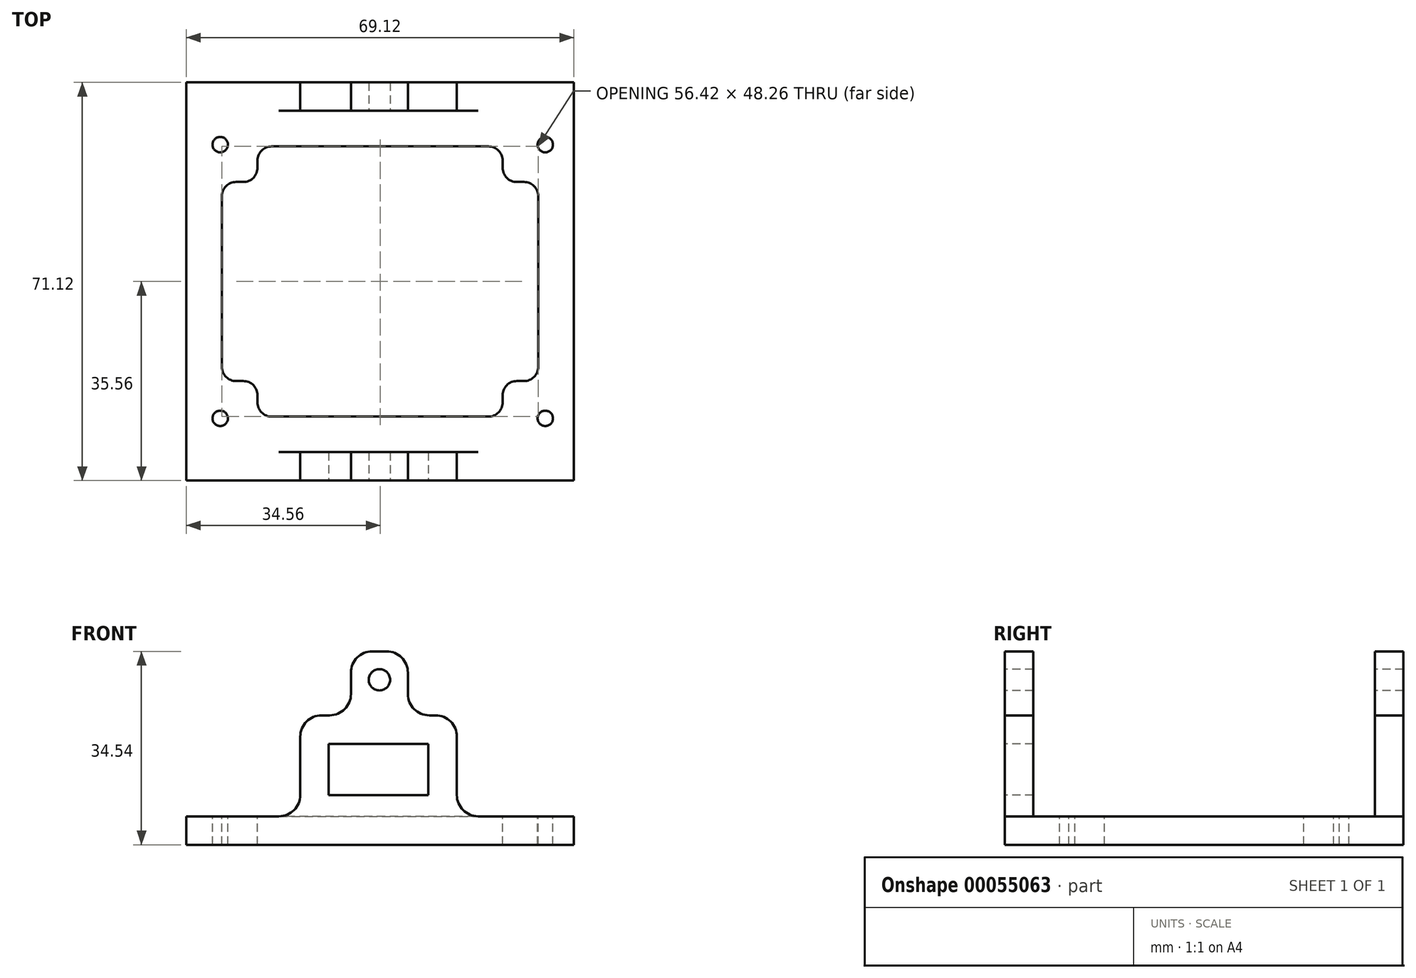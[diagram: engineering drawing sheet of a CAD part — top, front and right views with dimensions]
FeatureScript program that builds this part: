
annotation { "Feature Type Name" : "Feature", "Feature Type Description" : "" }
export const myFeature = defineFeature(function(context is Context, id is Id, definition is map)
    precondition{}
    {
        {
            var Q0;
            Q0=qCreatedBy(makeId("Top.planeOp"),FACE);
            var sketch = newSketch(context, id + "F0", { "sketchPlane" : qUnion([Q0])});
            skLineSegment(sketch, "E0.bottom", {"start": v(0, 0) * mm, "end": v(85.1, 0) * mm, "construction": true});
            skLineSegment(sketch, "E0.top", {"start": v(0, 55.88) * mm, "end": v(85.1, 55.88) * mm, "construction": true});
            skLineSegment(sketch, "E0.left", {"start": v(0, 0) * mm, "end": v(0, 55.88) * mm, "construction": true});
            skLineSegment(sketch, "E0.right", {"start": v(85.1, 0) * mm, "end": v(85.1, 55.88) * mm, "construction": true});
            skLineSegment(sketch, "E1", {"start": v(85.1, 54.61) * mm, "end": v(87.38, 54.61) * mm, "construction": true});
            skLineSegment(sketch, "E2", {"start": v(87.38, 54.61) * mm, "end": v(87.38, 2.29) * mm, "construction": true});
            skLineSegment(sketch, "E3", {"start": v(87.38, 2.29) * mm, "end": v(85.1, 2.29) * mm, "construction": true});
            skLineSegment(sketch, "E4", {"start": v(57.02, 0) * mm, "end": v(57.02, -2.29) * mm, "construction": true});
            skLineSegment(sketch, "E5", {"start": v(57.02, -2.29) * mm, "end": v(50.17, -2.29) * mm, "construction": true});
            skLineSegment(sketch, "E6", {"start": v(50.17, -2.29) * mm, "end": v(50.17, 0) * mm, "construction": true});
            skLineSegment(sketch, "E7", {"start": v(39.37, 0) * mm, "end": v(39.37, -0.76) * mm, "construction": true});
            skLineSegment(sketch, "E8", {"start": v(39.37, -0.76) * mm, "end": v(24.13, -0.76) * mm, "construction": true});
            skLineSegment(sketch, "E9", {"start": v(24.13, -0.76) * mm, "end": v(24.13, 0) * mm, "construction": true});
            skLineSegment(sketch, "E10", {"start": v(14.99, 0) * mm, "end": v(14.99, -1.27) * mm, "construction": true});
            skLineSegment(sketch, "E11", {"start": v(14.99, -1.27) * mm, "end": v(6.86, -1.27) * mm, "construction": true});
            skLineSegment(sketch, "E12", {"start": v(6.86, -1.27) * mm, "end": v(6.86, 0) * mm, "construction": true});
            skLineSegment(sketch, "E13", {"start": v(0, 33.53) * mm, "end": v(-2.54, 33.53) * mm, "construction": true});
            skLineSegment(sketch, "E14", {"start": v(-2.54, 33.53) * mm, "end": v(-2.54, 22.35) * mm, "construction": true});
            skLineSegment(sketch, "E15", {"start": v(-2.54, 22.35) * mm, "end": v(0, 22.35) * mm, "construction": true});
            skCircle(sketch, "E16", {"center": v(3.5, 52.38) * mm, "radius": 1.38 * mm});
            skCircle(sketch, "E17", {"center": v(3.5, 3.5) * mm, "radius": 1.38 * mm});
            skCircle(sketch, "E18", {"center": v(61.5, 3.5) * mm, "radius": 1.38 * mm});
            skCircle(sketch, "E19", {"center": v(61.5, 52.38) * mm, "radius": 1.38 * mm});
            skLineSegment(sketch, "E20.bottom", {"start": v(-2.54, -2.54) * mm, "end": v(87.63, -2.54) * mm});
            skLineSegment(sketch, "E20.top", {"start": v(-2.54, 58.42) * mm, "end": v(87.63, 58.42) * mm});
            skLineSegment(sketch, "E20.left", {"start": v(-2.54, -2.54) * mm, "end": v(-2.54, 58.42) * mm});
            skLineSegment(sketch, "E20.right", {"start": v(87.63, -2.54) * mm, "end": v(87.63, 58.42) * mm});
            skLineSegment(sketch, "E21.0", {"start": v(-7.62, -7.62) * mm, "end": v(92.71, -7.62) * mm});
            skLineSegment(sketch, "E21.1", {"start": v(-7.62, -7.62) * mm, "end": v(-7.62, 63.5) * mm});
            skLineSegment(sketch, "E21.2", {"start": v(-7.62, 63.5) * mm, "end": v(92.71, 63.5) * mm});
            skLineSegment(sketch, "E21.3", {"start": v(92.71, -7.62) * mm, "end": v(92.71, 63.5) * mm});
            skSolve(sketch);
        }
        {
            var Q0;
            Q0=makeQuery(id+"F0.imprint","IMPRINT",FACE,{"disambiguationData":[TD([[makeQuery(id+"F0.imprint","IMPRINT",EDGE,{"derivedFrom":sQuery(id+"F0.wireOp",EDGE,"E20.bottom")}),-1.0]])]});
            extrude(context, id + "F1", {"entities" : qUnion([Q0]), "oppositeDirection" : true, "depth" : 5.08 * mm});
        }
        {
            var Q0;
            Q0=makeQuery(id+"F1.opExtrude","CAP_FACE",FACE,{"disambiguationData":[OSD([sQuery(id+"F0.wireOp",EDGE,"E20.bottom"),sQuery(id+"F0.wireOp",EDGE,"E20.top"),sQuery(id+"F0.wireOp",EDGE,"E20.left"),sQuery(id+"F0.wireOp",EDGE,"E20.right"),sQuery(id+"F0.wireOp",EDGE,"E21.0"),sQuery(id+"F0.wireOp",EDGE,"E21.1"),sQuery(id+"F0.wireOp",EDGE,"E21.2"),sQuery(id+"F0.wireOp",EDGE,"E21.3")])],"isStart":false});
            var sketch = newSketch(context, id + "F2", { "sketchPlane" : qUnion([Q0])});
            skLineSegment(sketch, "E22.bottom", {"start": v(-7.62, 7.62) * mm, "end": v(92.71, 7.62) * mm});
            skLineSegment(sketch, "E22.top", {"start": v(-7.62, -63.5) * mm, "end": v(92.71, -63.5) * mm});
            skLineSegment(sketch, "E22.left", {"start": v(-7.62, 7.62) * mm, "end": v(-7.62, -63.5) * mm});
            skLineSegment(sketch, "E22.right", {"start": v(92.71, 7.62) * mm, "end": v(92.71, -63.5) * mm});
            skSolve(sketch);
        }
        {
            var Q0;
            Q0=qSketchRegion(id+"F2",true);
            extrude(context, id + "F3", {"entities" : qUnion([Q0]), "operationType" : NewBodyOperationType.ADD, "depth" : 5.08 * mm});
        }
        {
            var Q0;
            Q0=makeQuery(id+"F0.imprint","IMPRINT",FACE,{"disambiguationData":[TD([[makeQuery(id+"F0.imprint","IMPRINT",EDGE,{"derivedFrom":sQuery(id+"F0.wireOp",EDGE,"E16")}),1.0]])]});
            var Q1;
            Q1=makeQuery(id+"F0.imprint","IMPRINT",FACE,{"disambiguationData":[TD([[makeQuery(id+"F0.imprint","IMPRINT",EDGE,{"derivedFrom":sQuery(id+"F0.wireOp",EDGE,"E19")}),1.0]])]});
            var Q2;
            Q2=makeQuery(id+"F0.imprint","IMPRINT",FACE,{"disambiguationData":[TD([[makeQuery(id+"F0.imprint","IMPRINT",EDGE,{"derivedFrom":sQuery(id+"F0.wireOp",EDGE,"E18")}),1.0]])]});
            var Q3;
            Q3=makeQuery(id+"F0.imprint","IMPRINT",FACE,{"disambiguationData":[TD([[makeQuery(id+"F0.imprint","IMPRINT",EDGE,{"derivedFrom":sQuery(id+"F0.wireOp",EDGE,"E17")}),1.0]])]});
            extrude(context, id + "F4", {"entities" : qUnion([Q0, Q1, Q2, Q3]), "operationType" : NewBodyOperationType.REMOVE, "oppositeDirection" : true, "depth" : 25.4 * mm});
        }
        {
            var Q0;
            Q0=makeQuery(id+"F3.opExtrude","CAP_FACE",FACE,{"disambiguationData":[OSD([sQuery(id+"F2.wireOp",EDGE,"E22.bottom"),sQuery(id+"F2.wireOp",EDGE,"E22.top"),sQuery(id+"F2.wireOp",EDGE,"E22.left"),sQuery(id+"F2.wireOp",EDGE,"E22.right")])],"isStart":true});
            var sketch = newSketch(context, id + "F5", { "sketchPlane" : qUnion([Q0])});
            skCircle(sketch, "E23", {"center": v(3.5, 52.38) * mm, "radius": 3.1 * mm});
            skCircle(sketch, "E24", {"center": v(61.5, 52.38) * mm, "radius": 3.1 * mm});
            skCircle(sketch, "E25", {"center": v(61.5, 3.5) * mm, "radius": 3.1 * mm});
            skCircle(sketch, "E26", {"center": v(3.5, 3.5) * mm, "radius": 3.1 * mm});
            skCircle(sketch, "E27", {"center": v(3.5, 52.38) * mm, "radius": 1.38 * mm});
            skCircle(sketch, "E28", {"center": v(3.5, 3.5) * mm, "radius": 1.38 * mm});
            skCircle(sketch, "E29", {"center": v(61.5, 3.5) * mm, "radius": 1.38 * mm});
            skCircle(sketch, "E30", {"center": v(61.5, 52.38) * mm, "radius": 1.38 * mm});
            skSolve(sketch);
        }
        {
            var Q0;
            Q0=qSketchRegion(id+"F5",true);
            extrude(context, id + "F6", {"entities" : qUnion([Q0]), "operationType" : NewBodyOperationType.ADD, "depth" : 3.56 * mm});
        }
        {
            var Q0;
            Q0=makeQuery(id+"F0.imprint","IMPRINT",FACE,{"disambiguationData":[TD([[makeQuery(id+"F0.imprint","IMPRINT",EDGE,{"derivedFrom":sQuery(id+"F0.wireOp",EDGE,"E20.bottom")}),-1.0]])]});
            extrude(context, id + "F7", {"entities" : qUnion([Q0]), "operationType" : NewBodyOperationType.ADD, "depth" : 37.6 * mm});
        }
        {
            var Q0;
            {var subQ0=sQuery(id+"F0.wireOp",EDGE,"E21.1");Q0=makeQuery(id+"F7.boolean.opBoolean","MERGE",FACE,{"derivedFrom":[makeQuery(id+"F3.boolean.opBoolean","MERGE",FACE,{"derivedFrom":[makeQuery(id+"F1.opExtrude","SWEPT_FACE",FACE,{"disambiguationData":[OSD([subQ0])]}),makeQuery(id+"F3.opExtrude","SWEPT_FACE",FACE,{"disambiguationData":[OSD([sQuery(id+"F2.wireOp",EDGE,"E22.left")])]})]}),makeQuery(id+"F7.opExtrude","SWEPT_FACE",FACE,{"disambiguationData":[OSD([subQ0])]})]});}
            var sketch = newSketch(context, id + "F8", { "sketchPlane" : qUnion([Q0])});
            skLineSegment(sketch, "E31.rect.bottom", {"start": v(-21.08, -3.81) * mm, "end": v(-34.8, -3.81) * mm});
            skLineSegment(sketch, "E31.rect.top", {"start": v(-21.08, -0.25) * mm, "end": v(-34.8, -0.25) * mm});
            skLineSegment(sketch, "E31.rect.left", {"start": v(-21.08, -3.8) * mm, "end": v(-21.08, -0.25) * mm});
            skLineSegment(sketch, "E31.rect.right", {"start": v(-34.8, -3.81) * mm, "end": v(-34.8, -0.25) * mm});
            skPoint(sketch, "E31.rect.middle", {"position": v(-27.94, -2.03) * mm});
            skLineSegment(sketch, "E32.bottom", {"start": v(-33.53, -1.52) * mm, "end": v(-22.35, -1.52) * mm, "construction": true});
            skLineSegment(sketch, "E32.top", {"start": v(-33.53, -2.54) * mm, "end": v(-22.35, -2.54) * mm, "construction": true});
            skLineSegment(sketch, "E32.left", {"start": v(-33.53, -1.52) * mm, "end": v(-33.53, -2.54) * mm, "construction": true});
            skLineSegment(sketch, "E32.right", {"start": v(-22.35, -1.52) * mm, "end": v(-22.35, -2.54) * mm, "construction": true});
            skSolve(sketch);
        }
        {
            var Q0;
            Q0=qSketchRegion(id+"F8",true);
            extrude(context, id + "F9", {"entities" : qUnion([Q0]), "operationType" : NewBodyOperationType.REMOVE, "endBound" : BoundingType.UP_TO_NEXT, "oppositeDirection" : true, "depth" : 25.4 * mm});
        }
        {
            var Q0;
            {var subQ0=sQuery(id+"F0.wireOp",EDGE,"E21.0");Q0=makeQuery(id+"F7.boolean.opBoolean","MERGE",FACE,{"derivedFrom":[makeQuery(id+"F3.boolean.opBoolean","MERGE",FACE,{"derivedFrom":[makeQuery(id+"F1.opExtrude","SWEPT_FACE",FACE,{"disambiguationData":[OSD([subQ0])]}),makeQuery(id+"F3.opExtrude","SWEPT_FACE",FACE,{"disambiguationData":[OSD([sQuery(id+"F2.wireOp",EDGE,"E22.bottom")])]})]}),makeQuery(id+"F7.opExtrude","SWEPT_FACE",FACE,{"disambiguationData":[OSD([subQ0])]})]});}
            var sketch = newSketch(context, id + "F10", { "sketchPlane" : qUnion([Q0])});
            skLineSegment(sketch, "E33.bottom", {"start": v(6.86, 3.18) * mm, "end": v(14.99, 3.18) * mm, "construction": true});
            skLineSegment(sketch, "E33.top", {"start": v(6.86, 0) * mm, "end": v(14.99, 0) * mm, "construction": true});
            skLineSegment(sketch, "E33.left", {"start": v(6.86, 3.18) * mm, "end": v(6.86, 0) * mm, "construction": true});
            skLineSegment(sketch, "E33.right", {"start": v(14.99, 3.18) * mm, "end": v(14.99, 0) * mm, "construction": true});
            skLineSegment(sketch, "E34.bottom", {"start": v(24.13, 6.6) * mm, "end": v(39.37, 6.6) * mm, "construction": true});
            skLineSegment(sketch, "E34.top", {"start": v(24.13, 0) * mm, "end": v(39.37, 0) * mm, "construction": true});
            skLineSegment(sketch, "E34.left", {"start": v(24.13, 6.6) * mm, "end": v(24.13, 0) * mm, "construction": true});
            skLineSegment(sketch, "E34.right", {"start": v(39.37, 6.6) * mm, "end": v(39.37, 0) * mm, "construction": true});
            skLineSegment(sketch, "E35.bottom", {"start": v(50.17, 6.35) * mm, "end": v(57.02, 6.35) * mm, "construction": true});
            skLineSegment(sketch, "E35.top", {"start": v(50.17, 0) * mm, "end": v(57.02, 0) * mm, "construction": true});
            skLineSegment(sketch, "E35.left", {"start": v(50.17, 6.35) * mm, "end": v(50.17, 0) * mm, "construction": true});
            skLineSegment(sketch, "E35.right", {"start": v(57.02, 6.35) * mm, "end": v(57.02, 0) * mm, "construction": true});
            skLineSegment(sketch, "E36.bottom", {"start": v(16.26, 4.45) * mm, "end": v(5.59, 4.45) * mm});
            skLineSegment(sketch, "E36.top", {"start": v(16.26, -1.27) * mm, "end": v(5.59, -1.27) * mm});
            skLineSegment(sketch, "E36.left", {"start": v(16.26, 4.45) * mm, "end": v(16.26, -1.27) * mm});
            skLineSegment(sketch, "E36.right", {"start": v(5.59, 4.45) * mm, "end": v(5.59, -1.27) * mm});
            skLineSegment(sketch, "E37.bottom", {"start": v(22.86, 7.87) * mm, "end": v(40.64, 7.87) * mm});
            skLineSegment(sketch, "E37.top", {"start": v(22.86, -1.27) * mm, "end": v(40.64, -1.27) * mm});
            skLineSegment(sketch, "E37.left", {"start": v(22.86, 7.87) * mm, "end": v(22.86, -1.27) * mm});
            skLineSegment(sketch, "E37.right", {"start": v(40.64, 7.87) * mm, "end": v(40.64, -1.27) * mm});
            skLineSegment(sketch, "E38.bottom", {"start": v(48.9, 7.62) * mm, "end": v(58.3, 7.62) * mm});
            skLineSegment(sketch, "E38.top", {"start": v(48.9, -1.27) * mm, "end": v(58.3, -1.27) * mm});
            skLineSegment(sketch, "E38.left", {"start": v(48.9, 7.62) * mm, "end": v(48.9, -1.27) * mm});
            skLineSegment(sketch, "E38.right", {"start": v(58.3, 7.62) * mm, "end": v(58.3, -1.27) * mm});
            skPoint(sketch, "E39", {"position": v(14.99, 1.59) * mm});
            skPoint(sketch, "E40", {"position": v(10.92, 0) * mm});
            skPoint(sketch, "E41", {"position": v(10.92, -1.27) * mm});
            skPoint(sketch, "E42", {"position": v(16.26, 1.59) * mm});
            skPoint(sketch, "E43", {"position": v(22.86, 3.3) * mm});
            skPoint(sketch, "E44", {"position": v(31.75, -1.27) * mm});
            skPoint(sketch, "E45", {"position": v(31.75, 0) * mm});
            skPoint(sketch, "E46", {"position": v(24.13, 3.3) * mm});
            skPoint(sketch, "E47", {"position": v(58.3, 3.18) * mm});
            skPoint(sketch, "E48", {"position": v(53.6, -1.27) * mm});
            skPoint(sketch, "E49", {"position": v(53.6, 0) * mm});
            skPoint(sketch, "E50", {"position": v(57.02, 3.18) * mm});
            skLineSegment(sketch, "E51", {"start": v(14.99, 0) * mm, "end": v(14.99, -1.27) * mm, "construction": true});
            skLineSegment(sketch, "E52", {"start": v(14.99, 0) * mm, "end": v(16.26, 0) * mm, "construction": true});
            skLineSegment(sketch, "E53", {"start": v(24.13, 0) * mm, "end": v(22.86, 0) * mm, "construction": true});
            skLineSegment(sketch, "E54", {"start": v(24.13, 0) * mm, "end": v(24.13, -1.27) * mm, "construction": true});
            skLineSegment(sketch, "E55", {"start": v(50.17, 0) * mm, "end": v(48.9, 0) * mm, "construction": true});
            skLineSegment(sketch, "E56", {"start": v(50.17, 0) * mm, "end": v(50.17, -1.27) * mm, "construction": true});
            skSolve(sketch);
        }
        {
            var Q0;
            Q0=qSketchRegion(id+"F10",true);
            extrude(context, id + "F11", {"entities" : qUnion([Q0]), "operationType" : NewBodyOperationType.REMOVE, "endBound" : BoundingType.UP_TO_NEXT, "oppositeDirection" : true, "depth" : 25.4 * mm});
        }
        {
            var Q0;
            {var subQ0=sQuery(id+"F0.wireOp",EDGE,"E21.3");Q0=makeQuery(id+"F7.boolean.opBoolean","MERGE",FACE,{"derivedFrom":[makeQuery(id+"F3.boolean.opBoolean","MERGE",FACE,{"derivedFrom":[makeQuery(id+"F1.opExtrude","SWEPT_FACE",FACE,{"disambiguationData":[OSD([subQ0])]}),makeQuery(id+"F3.opExtrude","SWEPT_FACE",FACE,{"disambiguationData":[OSD([sQuery(id+"F2.wireOp",EDGE,"E22.right")])]})]}),makeQuery(id+"F7.opExtrude","SWEPT_FACE",FACE,{"disambiguationData":[OSD([subQ0])]})]});}
            var sketch = newSketch(context, id + "F12", { "sketchPlane" : qUnion([Q0])});
            skLineSegment(sketch, "E57.bottom", {"start": v(2.54, 13.72) * mm, "end": v(18.54, 13.72) * mm, "construction": true});
            skLineSegment(sketch, "E57.top", {"start": v(2.54, 0) * mm, "end": v(18.54, 0) * mm, "construction": true});
            skLineSegment(sketch, "E57.left", {"start": v(2.54, 13.72) * mm, "end": v(2.54, 0) * mm, "construction": true});
            skLineSegment(sketch, "E57.right", {"start": v(18.54, 13.72) * mm, "end": v(18.54, 0) * mm, "construction": true});
            skLineSegment(sketch, "E58.bottom", {"start": v(21.44, 16.26) * mm, "end": v(36.68, 16.26) * mm, "construction": true});
            skLineSegment(sketch, "E58.top", {"start": v(21.44, 0) * mm, "end": v(36.68, 0) * mm, "construction": true});
            skLineSegment(sketch, "E58.left", {"start": v(21.44, 16.26) * mm, "end": v(21.44, 0) * mm, "construction": true});
            skLineSegment(sketch, "E58.right", {"start": v(36.68, 16.26) * mm, "end": v(36.68, 0) * mm, "construction": true});
            skLineSegment(sketch, "E59.bottom", {"start": v(39.22, 16.26) * mm, "end": v(54.46, 16.26) * mm, "construction": true});
            skLineSegment(sketch, "E59.top", {"start": v(39.22, 0) * mm, "end": v(54.46, 0) * mm, "construction": true});
            skLineSegment(sketch, "E59.left", {"start": v(39.22, 16.26) * mm, "end": v(39.22, 0) * mm, "construction": true});
            skLineSegment(sketch, "E59.right", {"start": v(54.46, 16.26) * mm, "end": v(54.46, 0) * mm, "construction": true});
            skLineSegment(sketch, "E60.bottom", {"start": v(1.9, 16.9) * mm, "end": v(55.73, 16.9) * mm});
            skLineSegment(sketch, "E60.top", {"start": v(1.9, -1.27) * mm, "end": v(55.73, -1.27) * mm});
            skLineSegment(sketch, "E60.left", {"start": v(1.9, 16.9) * mm, "end": v(1.9, -1.27) * mm});
            skLineSegment(sketch, "E60.right", {"start": v(55.73, 16.9) * mm, "end": v(55.73, -1.27) * mm});
            skSolve(sketch);
        }
        {
            var Q0;
            Q0=qSketchRegion(id+"F12",true);
            extrude(context, id + "F13", {"entities" : qUnion([Q0]), "operationType" : NewBodyOperationType.REMOVE, "endBound" : BoundingType.UP_TO_NEXT, "oppositeDirection" : true, "depth" : 25.4 * mm});
        }
        {
            var Q0;
            {var subQ0=sQuery(id+"F0.wireOp",EDGE,"E21.0");Q0=makeQuery(id+"F7.boolean.opBoolean","MERGE",FACE,{"derivedFrom":[makeQuery(id+"F3.boolean.opBoolean","MERGE",FACE,{"derivedFrom":[makeQuery(id+"F1.opExtrude","SWEPT_FACE",FACE,{"disambiguationData":[OSD([subQ0])]}),makeQuery(id+"F3.opExtrude","SWEPT_FACE",FACE,{"disambiguationData":[OSD([sQuery(id+"F2.wireOp",EDGE,"E22.bottom")])]})]}),makeQuery(id+"F7.opExtrude","SWEPT_FACE",FACE,{"disambiguationData":[OSD([subQ0])]})]});}
            var sketch = newSketch(context, id + "F14", { "sketchPlane" : qUnion([Q0])});
            skCircle(sketch, "E61", {"center": v(31.9, 19.3) * mm, "radius": 1.9 * mm});
            skSolve(sketch);
        }
        {
            var Q0;
            Q0=qSketchRegion(id+"F14",true);
            extrude(context, id + "F15", {"entities" : qUnion([Q0]), "operationType" : NewBodyOperationType.REMOVE, "endBound" : BoundingType.THROUGH_ALL, "oppositeDirection" : true, "depth" : 25.4 * mm});
        }
        {
            var Q0;
            {var subQ0=sQuery(id+"F0.wireOp",EDGE,"E21.0");Q0=makeQuery(id+"F7.boolean.opBoolean","MERGE",FACE,{"derivedFrom":[makeQuery(id+"F3.boolean.opBoolean","MERGE",FACE,{"derivedFrom":[makeQuery(id+"F1.opExtrude","SWEPT_FACE",FACE,{"disambiguationData":[OSD([subQ0])]}),makeQuery(id+"F3.opExtrude","SWEPT_FACE",FACE,{"disambiguationData":[OSD([sQuery(id+"F2.wireOp",EDGE,"E22.bottom")])]})]}),makeQuery(id+"F7.opExtrude","SWEPT_FACE",FACE,{"disambiguationData":[OSD([subQ0])]})]});}
            var sketch = newSketch(context, id + "F16", { "sketchPlane" : qUnion([Q0])});
            skLineSegment(sketch, "E62", {"start": v(66.58, -10.16) * mm, "end": v(66.58, -5.08) * mm});
            skLineSegment(sketch, "E63", {"start": v(-2.54, -10.16) * mm, "end": v(-2.54, -5.08) * mm});
            skLineSegment(sketch, "E64", {"start": v(-2.54, -10.16) * mm, "end": v(-7.62, -10.16) * mm});
            skLineSegment(sketch, "E65", {"start": v(-7.62, -10.16) * mm, "end": v(-7.62, 37.6) * mm});
            skLineSegment(sketch, "E66", {"start": v(-7.62, 37.6) * mm, "end": v(92.71, 37.6) * mm});
            skLineSegment(sketch, "E67", {"start": v(92.71, 37.6) * mm, "end": v(92.71, -10.16) * mm});
            skLineSegment(sketch, "E68", {"start": v(92.71, -10.16) * mm, "end": v(66.58, -10.16) * mm});
            skLineSegment(sketch, "E69", {"start": v(-2.54, -5.08) * mm, "end": v(13.97, -5.08) * mm});
            skLineSegment(sketch, "E70", {"start": v(17.78, -1.27) * mm, "end": v(17.78, 9.14) * mm});
            skLineSegment(sketch, "E71", {"start": v(21.6, 12.95) * mm, "end": v(23.01, 12.95) * mm});
            skLineSegment(sketch, "E72", {"start": v(26.82, 16.76) * mm, "end": v(26.82, 20.57) * mm});
            skLineSegment(sketch, "E73", {"start": v(30.63, 24.38) * mm, "end": v(33.17, 24.38) * mm});
            skLineSegment(sketch, "E74", {"start": v(36.98, 20.57) * mm, "end": v(36.98, 16.76) * mm});
            skLineSegment(sketch, "E75", {"start": v(40.8, 12.95) * mm, "end": v(41.91, 12.95) * mm});
            skLineSegment(sketch, "E76", {"start": v(45.72, 9.14) * mm, "end": v(45.72, -1.27) * mm});
            skLineSegment(sketch, "E77", {"start": v(49.53, -5.08) * mm, "end": v(66.58, -5.08) * mm});
            skCircle(sketch, "E78", {"center": v(31.9, 19.3) * mm, "radius": 5.08 * mm, "construction": true});
            skPoint(sketch, "E79.visualSharp", {"position": v(17.78, -5.08) * mm});
            skArc(sketch, "E79.filletArc", {"start": v(13.97, -5.08) * mm, "mid": v(16.66, -3.96) * mm, "end": v(17.78, -1.27) * mm});
            skPoint(sketch, "E80.visualSharp", {"position": v(17.78, 12.95) * mm});
            skArc(sketch, "E80.filletArc", {"start": v(21.6, 12.95) * mm, "mid": v(18.9, 11.84) * mm, "end": v(17.78, 9.14) * mm});
            skPoint(sketch, "E81.visualSharp", {"position": v(26.82, 12.95) * mm});
            skArc(sketch, "E81.filletArc", {"start": v(23.01, 12.95) * mm, "mid": v(25.7, 14.07) * mm, "end": v(26.82, 16.76) * mm});
            skPoint(sketch, "E82.visualSharp", {"position": v(26.82, 24.38) * mm});
            skArc(sketch, "E82.filletArc", {"start": v(30.63, 24.38) * mm, "mid": v(27.94, 23.27) * mm, "end": v(26.82, 20.57) * mm});
            skPoint(sketch, "E83.visualSharp", {"position": v(36.98, 24.38) * mm});
            skArc(sketch, "E83.filletArc", {"start": v(36.98, 20.57) * mm, "mid": v(35.87, 23.27) * mm, "end": v(33.17, 24.38) * mm});
            skPoint(sketch, "E84.visualSharp", {"position": v(36.98, 12.95) * mm});
            skArc(sketch, "E84.filletArc", {"start": v(36.98, 16.76) * mm, "mid": v(38.1, 14.07) * mm, "end": v(40.8, 12.95) * mm});
            skPoint(sketch, "E85.visualSharp", {"position": v(45.72, 12.95) * mm});
            skArc(sketch, "E85.filletArc", {"start": v(45.72, 9.14) * mm, "mid": v(44.6, 11.84) * mm, "end": v(41.91, 12.95) * mm});
            skPoint(sketch, "E86.visualSharp", {"position": v(45.72, -5.08) * mm});
            skArc(sketch, "E86.filletArc", {"start": v(45.72, -1.27) * mm, "mid": v(46.84, -3.96) * mm, "end": v(49.53, -5.08) * mm});
            skSolve(sketch);
        }
        {
            var Q0;
            Q0 = qSketchRegion(id + "F16", true);
            extrude(context, id + "F17", {"entities" : qUnion([Q0]), "operationType" : NewBodyOperationType.REMOVE, "endBound" : BoundingType.THROUGH_ALL, "oppositeDirection" : true, "depth" : 25.4 * mm});
        }
        {
            var Q0;
            Q0=makeQuery(id+"F3.opExtrude","CAP_FACE",FACE,{"disambiguationData":[OSD([sQuery(id+"F2.wireOp",EDGE,"E22.bottom"),sQuery(id+"F2.wireOp",EDGE,"E22.top"),sQuery(id+"F2.wireOp",EDGE,"E22.left"),sQuery(id+"F2.wireOp",EDGE,"E22.right")])],"isStart":true});
            var sketch = newSketch(context, id + "F18", { "sketchPlane" : qUnion([Q0])});
            skLineSegment(sketch, "E87", {"start": v(57.7, 10.16) * mm, "end": v(56.42, 10.16) * mm});
            skLineSegment(sketch, "E88", {"start": v(53.88, 7.62) * mm, "end": v(53.88, 6.35) * mm});
            skLineSegment(sketch, "E89", {"start": v(51.34, 3.81) * mm, "end": v(12.7, 3.8) * mm});
            skLineSegment(sketch, "E90", {"start": v(10.16, 6.35) * mm, "end": v(10.16, 7.62) * mm});
            skLineSegment(sketch, "E91", {"start": v(7.62, 10.16) * mm, "end": v(6.35, 10.16) * mm});
            skLineSegment(sketch, "E92", {"start": v(3.81, 12.7) * mm, "end": v(3.81, 43.18) * mm});
            skLineSegment(sketch, "E93", {"start": v(6.35, 45.72) * mm, "end": v(7.62, 45.72) * mm});
            skLineSegment(sketch, "E94", {"start": v(10.16, 48.26) * mm, "end": v(10.16, 49.53) * mm});
            skLineSegment(sketch, "E95", {"start": v(12.7, 52.07) * mm, "end": v(51.34, 52.07) * mm});
            skLineSegment(sketch, "E96", {"start": v(53.88, 49.53) * mm, "end": v(53.88, 48.26) * mm});
            skLineSegment(sketch, "E97", {"start": v(56.42, 45.72) * mm, "end": v(57.7, 45.72) * mm});
            skLineSegment(sketch, "E98", {"start": v(60.23, 43.18) * mm, "end": v(60.23, 12.7) * mm});
            skLineSegment(sketch, "E99", {"start": v(3.8, 10.16) * mm, "end": v(-2.54, 10.16) * mm, "construction": true});
            skLineSegment(sketch, "E100", {"start": v(60.23, 10.16) * mm, "end": v(66.58, 10.16) * mm, "construction": true});
            skLineSegment(sketch, "E101", {"start": v(53.88, 52.07) * mm, "end": v(53.88, 58.42) * mm, "construction": true});
            skLineSegment(sketch, "E102", {"start": v(53.88, 3.8) * mm, "end": v(53.88, -2.54) * mm, "construction": true});
            skPoint(sketch, "E103.visualSharp", {"position": v(3.81, 45.72) * mm});
            skArc(sketch, "E103.filletArc", {"start": v(6.35, 45.72) * mm, "mid": v(4.55, 44.98) * mm, "end": v(3.8, 43.18) * mm});
            skPoint(sketch, "E104.visualSharp", {"position": v(10.16, 45.72) * mm});
            skArc(sketch, "E104.filletArc", {"start": v(7.62, 45.72) * mm, "mid": v(9.42, 46.46) * mm, "end": v(10.16, 48.26) * mm});
            skPoint(sketch, "E105.visualSharp", {"position": v(10.16, 52.07) * mm});
            skArc(sketch, "E105.filletArc", {"start": v(12.7, 52.07) * mm, "mid": v(10.9, 51.33) * mm, "end": v(10.16, 49.53) * mm});
            skPoint(sketch, "E106.visualSharp", {"position": v(53.88, 52.07) * mm});
            skArc(sketch, "E106.filletArc", {"start": v(53.88, 49.53) * mm, "mid": v(53.14, 51.33) * mm, "end": v(51.34, 52.07) * mm});
            skPoint(sketch, "E107.visualSharp", {"position": v(53.88, 45.72) * mm});
            skArc(sketch, "E107.filletArc", {"start": v(53.88, 48.26) * mm, "mid": v(54.62, 46.46) * mm, "end": v(56.42, 45.72) * mm});
            skPoint(sketch, "E108.visualSharp", {"position": v(60.23, 45.72) * mm});
            skArc(sketch, "E108.filletArc", {"start": v(60.23, 43.18) * mm, "mid": v(59.49, 44.98) * mm, "end": v(57.7, 45.72) * mm});
            skPoint(sketch, "E109.visualSharp", {"position": v(60.23, 10.16) * mm});
            skArc(sketch, "E109.filletArc", {"start": v(57.7, 10.16) * mm, "mid": v(59.49, 10.9) * mm, "end": v(60.23, 12.7) * mm});
            skPoint(sketch, "E110.visualSharp", {"position": v(53.88, 10.16) * mm});
            skArc(sketch, "E110.filletArc", {"start": v(56.42, 10.16) * mm, "mid": v(54.62, 9.42) * mm, "end": v(53.88, 7.62) * mm});
            skPoint(sketch, "E111.visualSharp", {"position": v(53.88, 3.8) * mm});
            skArc(sketch, "E111.filletArc", {"start": v(51.34, 3.81) * mm, "mid": v(53.14, 4.55) * mm, "end": v(53.88, 6.35) * mm});
            skPoint(sketch, "E112.visualSharp", {"position": v(10.16, 3.8) * mm});
            skArc(sketch, "E112.filletArc", {"start": v(10.16, 6.35) * mm, "mid": v(10.9, 4.55) * mm, "end": v(12.7, 3.8) * mm});
            skPoint(sketch, "E113.visualSharp", {"position": v(10.16, 10.16) * mm});
            skArc(sketch, "E113.filletArc", {"start": v(10.16, 7.62) * mm, "mid": v(9.42, 9.42) * mm, "end": v(7.62, 10.16) * mm});
            skPoint(sketch, "E114.visualSharp", {"position": v(3.8, 10.16) * mm});
            skArc(sketch, "E114.filletArc", {"start": v(3.81, 12.7) * mm, "mid": v(4.55, 10.9) * mm, "end": v(6.35, 10.16) * mm});
            skSolve(sketch);
        }
        {
            var Q0;
            Q0 = qSketchRegion(id + "F18", true);
            extrude(context, id + "F19", {"entities" : qUnion([Q0]), "operationType" : NewBodyOperationType.REMOVE, "endBound" : BoundingType.UP_TO_NEXT, "oppositeDirection" : true, "depth" : 25.4 * mm});
        }
    });
